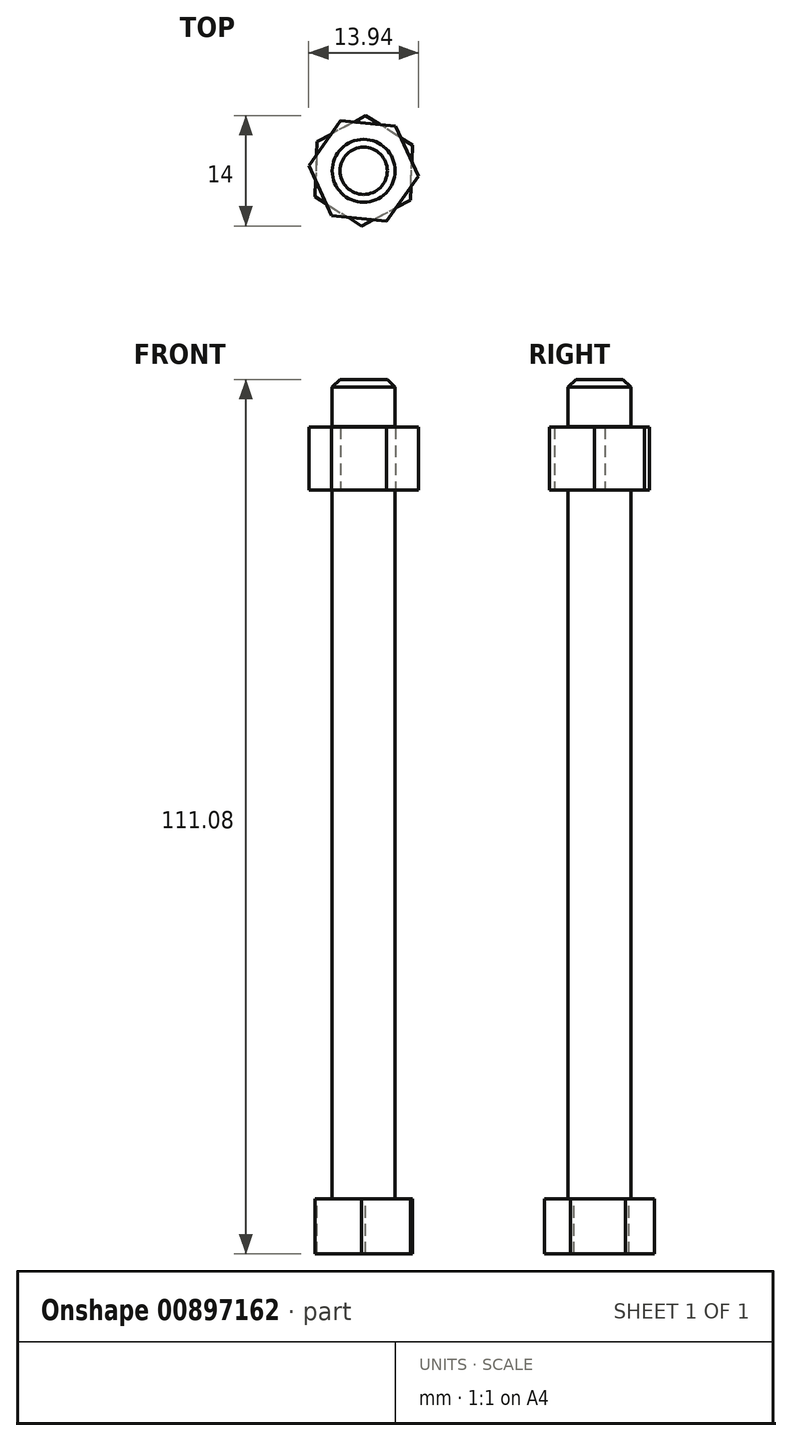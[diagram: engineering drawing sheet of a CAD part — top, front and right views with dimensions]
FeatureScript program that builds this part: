
annotation { "Feature Type Name" : "Feature", "Feature Type Description" : "" }
export const myFeature = defineFeature(function(context is Context, id is Id, definition is map)
    precondition{}
    {
        {
            var Q0;
            Q0=qCreatedBy(makeId("Front.planeOp"),FACE);
            var sketch = newSketch(context, id + "F0", { "sketchPlane" : qUnion([Q0])});
            skLineSegment(sketch, "E0", {"start": v(4, 90) * mm, "end": v(0, 90) * mm});
            skLineSegment(sketch, "E1", {"start": v(0, 90) * mm, "end": v(0, 65) * mm});
            skLineSegment(sketch, "E2", {"start": v(0, 65) * mm, "end": v(0, 0) * mm});
            skLineSegment(sketch, "E3", {"start": v(0, 0) * mm, "end": v(4, 0) * mm});
            skLineSegment(sketch, "E4", {"start": v(4, 0) * mm, "end": v(4, 90) * mm});
            skSolve(sketch);
        }
        {
            var Q0;
            Q0 = qSketchRegion(id + "F0", true);
            var Q1;
            Q1=sQuery(id+"F0.wireOp",EDGE,"E2");
            revolve(context, id + "F1", {"surfaceOperationType" : NewSurfaceOperationType.NEW, "entities" : qUnion([Q0]), "axis" : qUnion([Q1]), "revolveType" : RevolveType.FULL});
        }
        {
            var Q0;
            Q0=makeQuery(id+"F1.opRevolve","SWEPT_FACE",FACE,{"disambiguationData":[OSD([sQuery(id+"F0.wireOp",EDGE,"E3")])]});
            var sketch = newSketch(context, id + "F2", { "sketchPlane" : qUnion([Q0])});
            skLineSegment(sketch, "E5.0", {"start": v(5.93, 3.73) * mm, "end": v(6.19, -3.27) * mm});
            skLineSegment(sketch, "E5.1", {"start": v(6.19, -3.27) * mm, "end": v(0.26, -7) * mm});
            skLineSegment(sketch, "E5.2", {"start": v(0.26, -7) * mm, "end": v(-5.93, -3.73) * mm});
            skLineSegment(sketch, "E5.3", {"start": v(-5.93, -3.73) * mm, "end": v(-6.19, 3.27) * mm});
            skLineSegment(sketch, "E5.4", {"start": v(-6.19, 3.27) * mm, "end": v(-0.26, 7) * mm});
            skLineSegment(sketch, "E5.5", {"start": v(-0.26, 7) * mm, "end": v(5.93, 3.73) * mm});
            skSolve(sketch);
        }
        {
            var Q0;
            Q0 = qSketchRegion(id + "F2", true);
            extrude(context, id + "F3", {"entities" : qUnion([Q0]), "operationType" : NewBodyOperationType.ADD, "depth" : 7 * mm, "offsetDistance" : 25 * mm});
        }
        {
            var Q0;
            Q0=makeQuery(id+"F1.opRevolve","SWEPT_FACE",FACE,{"disambiguationData":[OSD([sQuery(id+"F0.wireOp",EDGE,"E0")])]});
            var sketch = newSketch(context, id + "F4", { "sketchPlane" : qUnion([Q0])});
            skLineSegment(sketch, "E6.0", {"start": v(4.06, 5.7) * mm, "end": v(6.97, -0.66) * mm});
            skLineSegment(sketch, "E6.1", {"start": v(6.97, -0.66) * mm, "end": v(2.9, -6.37) * mm});
            skLineSegment(sketch, "E6.2", {"start": v(2.9, -6.37) * mm, "end": v(-4.06, -5.7) * mm});
            skLineSegment(sketch, "E6.3", {"start": v(-4.06, -5.7) * mm, "end": v(-6.97, 0.66) * mm});
            skLineSegment(sketch, "E6.4", {"start": v(-6.97, 0.66) * mm, "end": v(-2.9, 6.37) * mm});
            skLineSegment(sketch, "E6.5", {"start": v(-2.9, 6.37) * mm, "end": v(4.06, 5.7) * mm});
            skSolve(sketch);
        }
        {
            var Q0;
            Q0 = qSketchRegion(id + "F4", true);
            extrude(context, id + "F5", {"entities" : qUnion([Q0]), "operationType" : NewBodyOperationType.ADD, "depth" : 8 * mm, "offsetDistance" : 25 * mm});
        }
        {
            var Q0;
            Q0=qCreatedBy(makeId("Front.planeOp"),FACE);
            var sketch = newSketch(context, id + "F6", { "sketchPlane" : qUnion([Q0])});
            skLineSegment(sketch, "E7", {"start": v(0, 98.08) * mm, "end": v(4, 98.08) * mm});
            skLineSegment(sketch, "E8", {"start": v(4, 98.08) * mm, "end": v(4, 103.08) * mm});
            skLineSegment(sketch, "E9", {"start": v(3, 104.08) * mm, "end": v(0, 104.08) * mm});
            skLineSegment(sketch, "E10", {"start": v(0, 104.08) * mm, "end": v(0, 98.08) * mm});
            skPoint(sketch, "E11.orphan", {"position": v(-4, 104.08) * mm});
            skPoint(sketch, "E12.start.orphan", {"position": v(-4, 98.08) * mm});
            skLineSegment(sketch, "E13", {"start": v(4, 103.08) * mm, "end": v(3, 104.08) * mm});
            skPoint(sketch, "E14.orphan", {"position": v(4, 104.08) * mm});
            skSolve(sketch);
        }
        {
            var Q0;
            Q0 = qSketchRegion(id + "F6", true);
            var Q1;
            Q1=sQuery(id+"F6.wireOp",EDGE,"E10");
            revolve(context, id + "F7", {"surfaceOperationType" : NewSurfaceOperationType.NEW, "entities" : qUnion([Q0]), "axis" : qUnion([Q1]), "revolveType" : RevolveType.FULL});
        }
    });
